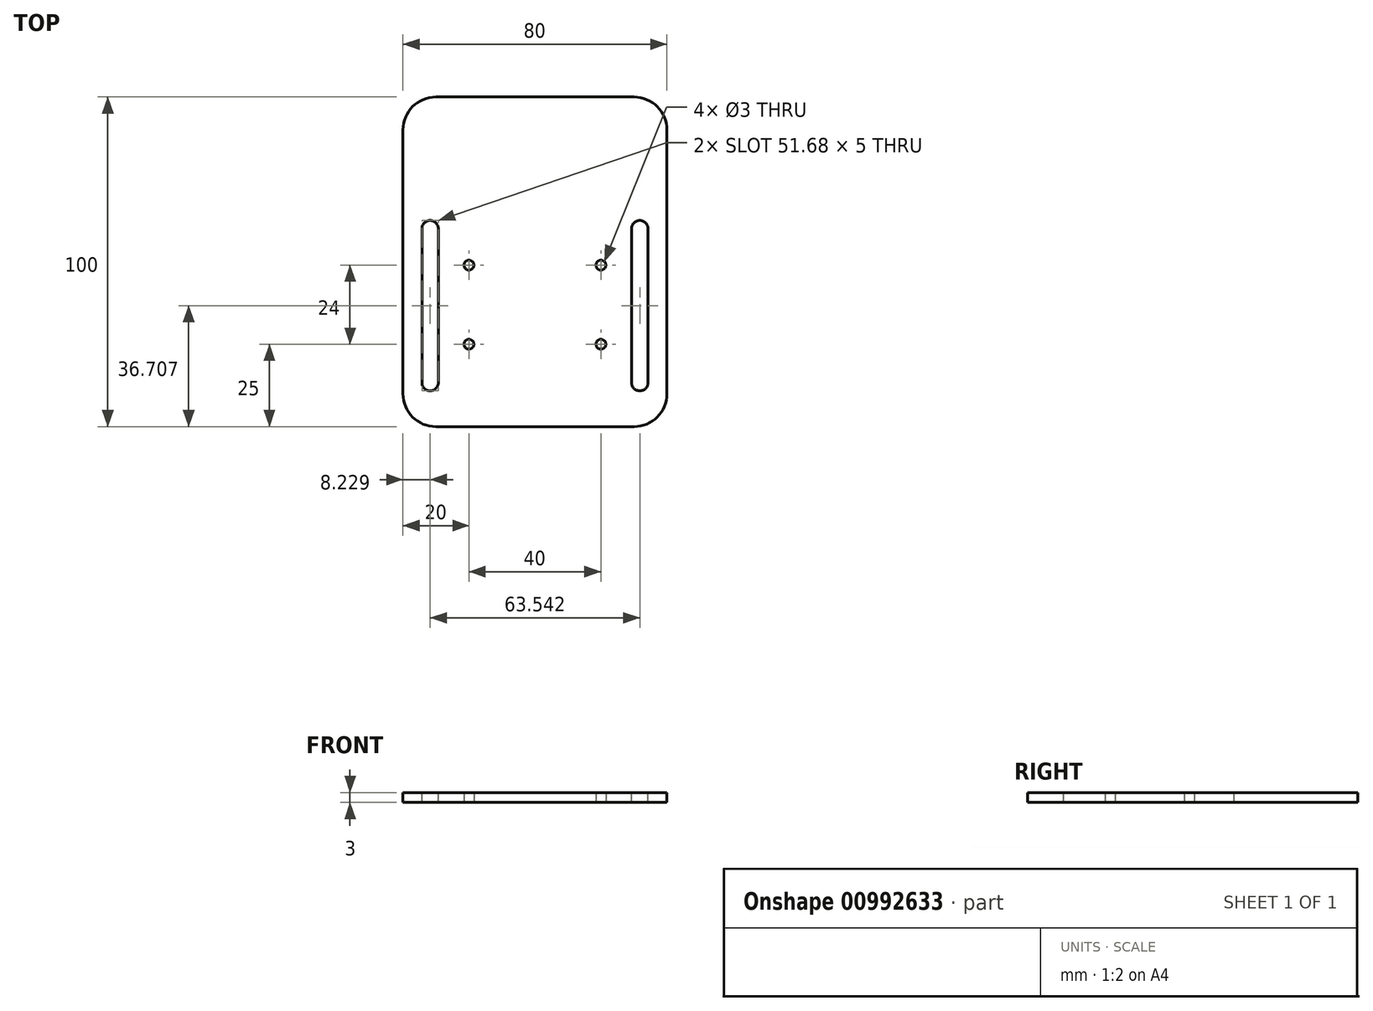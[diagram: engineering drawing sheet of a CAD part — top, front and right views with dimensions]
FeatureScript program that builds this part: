
annotation { "Feature Type Name" : "Feature", "Feature Type Description" : "" }
export const myFeature = defineFeature(function(context is Context, id is Id, definition is map)
    precondition{}
    {
        {
            var Q0;
            Q0=qCreatedBy(makeId("Top.planeOp"),FACE);
            var sketch = newSketch(context, id + "F0", { "sketchPlane" : qUnion([Q0])});
            skLineSegment(sketch, "E0.bottom", {"start": v(0, 0) * mm, "end": v(40, 0) * mm});
            skLineSegment(sketch, "E0.top", {"start": v(0, 100) * mm, "end": v(40, 100) * mm});
            skLineSegment(sketch, "E0.left", {"start": v(0, 0) * mm, "end": v(0, 100) * mm});
            skLineSegment(sketch, "E0.right", {"start": v(40, 0) * mm, "end": v(40, 100) * mm});
            skSolve(sketch);
        }
        {
            var Q0;
            Q0=makeQuery(id+"F0.imprint","IMPRINT",FACE,{"disambiguationData":[TD([[makeQuery(id+"F0.imprint","IMPRINT",EDGE,{"derivedFrom":sQuery(id+"F0.wireOp",EDGE,"E0.bottom")}),1.0]])]});
            extrude(context, id + "F1", {"entities" : qUnion([Q0]), "depth" : 3 * mm, "offsetDistance" : 25 * mm});
        }
        {
            var Q0;
            Q0=qCreatedBy(makeId("Top.planeOp"),FACE);
            var sketch = newSketch(context, id + "F2", { "sketchPlane" : qUnion([Q0])});
            skLineSegment(sketch, "E1", {"start": v(20, 25) * mm, "end": v(20, 49) * mm});
            skSolve(sketch);
        }
        {
            var Q0;
            Q0=sQuery(id+"F2.wireOp",VERTEX,"E1.end");
            var Q1;
            Q1=sQuery(id+"F2.wireOp",VERTEX,"E1.start");
            var Q2;
            Q2=makeQuery(id+"F1.opExtrude","SWEPT_BODY",BODY,{"disambiguationData":[OSD([sQuery(id+"F0.wireOp",EDGE,"E0.bottom"),sQuery(id+"F0.wireOp",EDGE,"E0.top"),sQuery(id+"F0.wireOp",EDGE,"E0.left"),sQuery(id+"F0.wireOp",EDGE,"E0.right")])]});
            hole(context, id + "F3", {"style" : HoleStyle.SIMPLE, "endStyle" : HoleEndStyle.THROUGH, "oppositeDirection" : true, "holeDiameter" : 3 * mm, "majorDiameter" : 5 * mm, "isTappedThrough" : true, "tappedDepth" : 12 * mm, "tapClearance" : 3, "locations" : qUnion([Q0, Q1]), "scope" : qUnion([Q2])});
        }
        {
            var Q0;
            Q0=makeQuery(id+"F1.opExtrude","CAP_FACE",FACE,{"disambiguationData":[OSD([sQuery(id+"F0.wireOp",EDGE,"E0.bottom"),sQuery(id+"F0.wireOp",EDGE,"E0.top"),sQuery(id+"F0.wireOp",EDGE,"E0.left"),sQuery(id+"F0.wireOp",EDGE,"E0.right")])],"isStart":false});
            var sketch = newSketch(context, id + "F4", { "sketchPlane" : qUnion([Q0])});
            skLineSegment(sketch, "E2", {"start": v(31.77, 60.05) * mm, "end": v(31.77, 13.36) * mm});
            skArc(sketch, "E3.0.startCap", {"start": v(29.27, 60.05) * mm, "mid": v(31.77, 62.55) * mm, "end": v(34.27, 60.05) * mm});
            skArc(sketch, "E3.0.endCap", {"start": v(34.27, 13.36) * mm, "mid": v(31.77, 10.86) * mm, "end": v(29.27, 13.36) * mm});
            skLineSegment(sketch, "E3.0.left", {"start": v(34.27, 60.05) * mm, "end": v(34.27, 13.36) * mm});
            skLineSegment(sketch, "E3.0.right", {"start": v(29.27, 60.05) * mm, "end": v(29.27, 13.36) * mm});
            skSolve(sketch);
        }
        {
            var Q0;
            Q0 = qSketchRegion(id + "F4", true);
            extrude(context, id + "F5", {"entities" : qUnion([Q0]), "operationType" : NewBodyOperationType.REMOVE, "oppositeDirection" : true, "depth" : 25 * mm, "offsetDistance" : 25 * mm});
        }
        {
            var Q0;
            Q0=makeQuery(id+"F1.opExtrude","SWEPT_EDGE",EDGE,{"disambiguationData":[OSD([sQuery(id+"F0.wireOp",EDGE,"E0.top"),sQuery(id+"F0.wireOp",EDGE,"E0.right")])]});
            var Q1;
            Q1=makeQuery(id+"F1.opExtrude","SWEPT_EDGE",EDGE,{"disambiguationData":[OSD([sQuery(id+"F0.wireOp",EDGE,"E0.bottom"),sQuery(id+"F0.wireOp",EDGE,"E0.right")])]});
            fillet(context, id + "F6", {"entities" : qUnion([Q0, Q1]), "radius" : 10 * mm, "tangentPropagation" : true, "allowEdgeOverflow" : false});
        }
        {
            var Q0;
            Q0=makeQuery(id+"F1.opExtrude","SWEPT_BODY",BODY,{"disambiguationData":[OSD([sQuery(id+"F0.wireOp",EDGE,"E0.bottom"),sQuery(id+"F0.wireOp",EDGE,"E0.top"),sQuery(id+"F0.wireOp",EDGE,"E0.left"),sQuery(id+"F0.wireOp",EDGE,"E0.right")])]});
            var Q1;
            Q1=qCreatedBy(makeId("Right.planeOp"),FACE);
            mirror(context, id + "F7", {"operationType" : NewBodyOperationType.ADD, "entities" : qUnion([Q0]), "mirrorPlane" : qUnion([Q1])});
        }
    });
